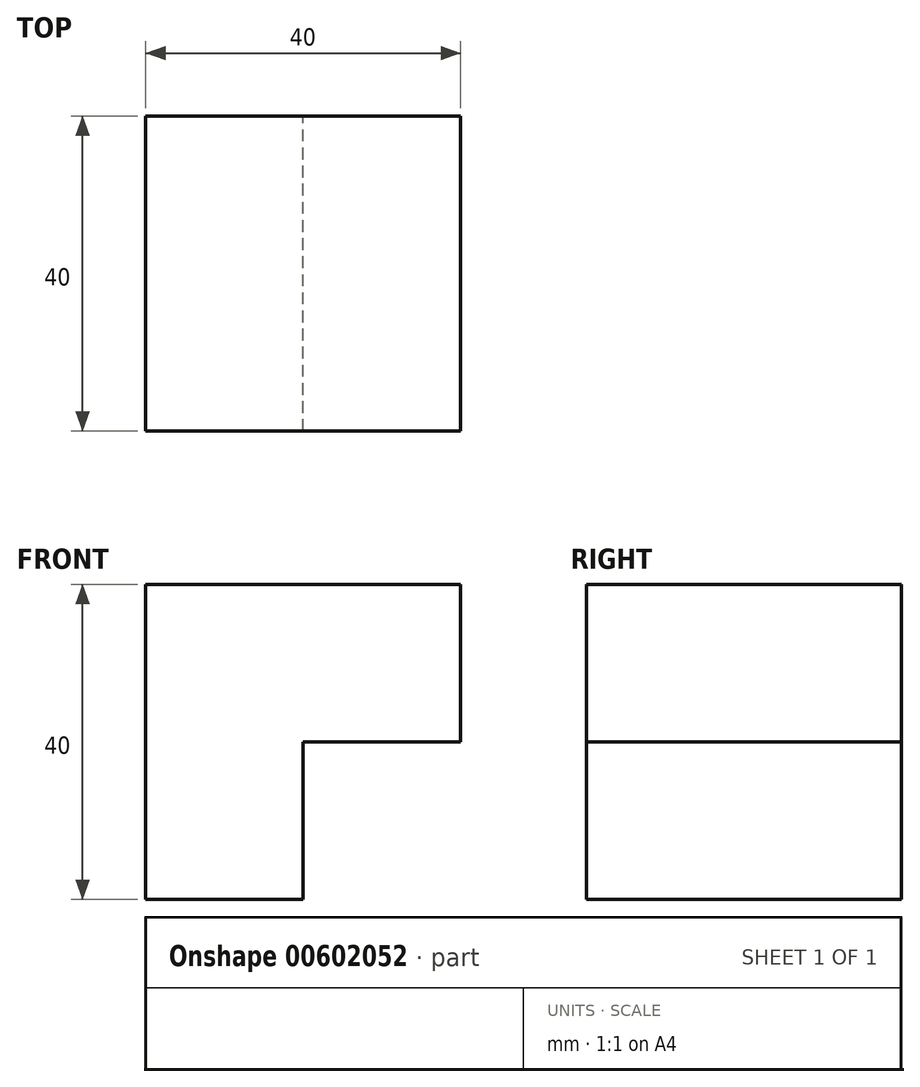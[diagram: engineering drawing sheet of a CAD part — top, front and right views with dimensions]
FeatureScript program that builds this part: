
annotation { "Feature Type Name" : "Feature", "Feature Type Description" : "" }
export const myFeature = defineFeature(function(context is Context, id is Id, definition is map)
    precondition{}
    {
        {
            var Q0;
            Q0=qCreatedBy(makeId("Front.planeOp"),FACE);
            var sketch = newSketch(context, id + "F0", { "sketchPlane" : qUnion([Q0])});
            skLineSegment(sketch, "E0", {"start": v(-58.85, 23.56) * mm, "end": v(-58.85, -16.44) * mm});
            skLineSegment(sketch, "E1", {"start": v(-58.85, -16.44) * mm, "end": v(-38.85, -16.44) * mm});
            skLineSegment(sketch, "E2", {"start": v(-38.85, -16.44) * mm, "end": v(-38.85, 3.56) * mm});
            skLineSegment(sketch, "E3", {"start": v(-38.85, 3.56) * mm, "end": v(-18.85, 3.56) * mm});
            skLineSegment(sketch, "E4", {"start": v(-18.85, 3.56) * mm, "end": v(-18.85, 23.56) * mm});
            skLineSegment(sketch, "E5", {"start": v(-18.85, 23.56) * mm, "end": v(-58.85, 23.56) * mm});
            skSolve(sketch);
        }
        {
            var Q0;
            Q0 = qSketchRegion(id + "F0", true);
            extrude(context, id + "F1", {"entities" : qUnion([Q0]), "depth" : 40 * mm, "offsetDistance" : 25 * mm});
        }
    });
